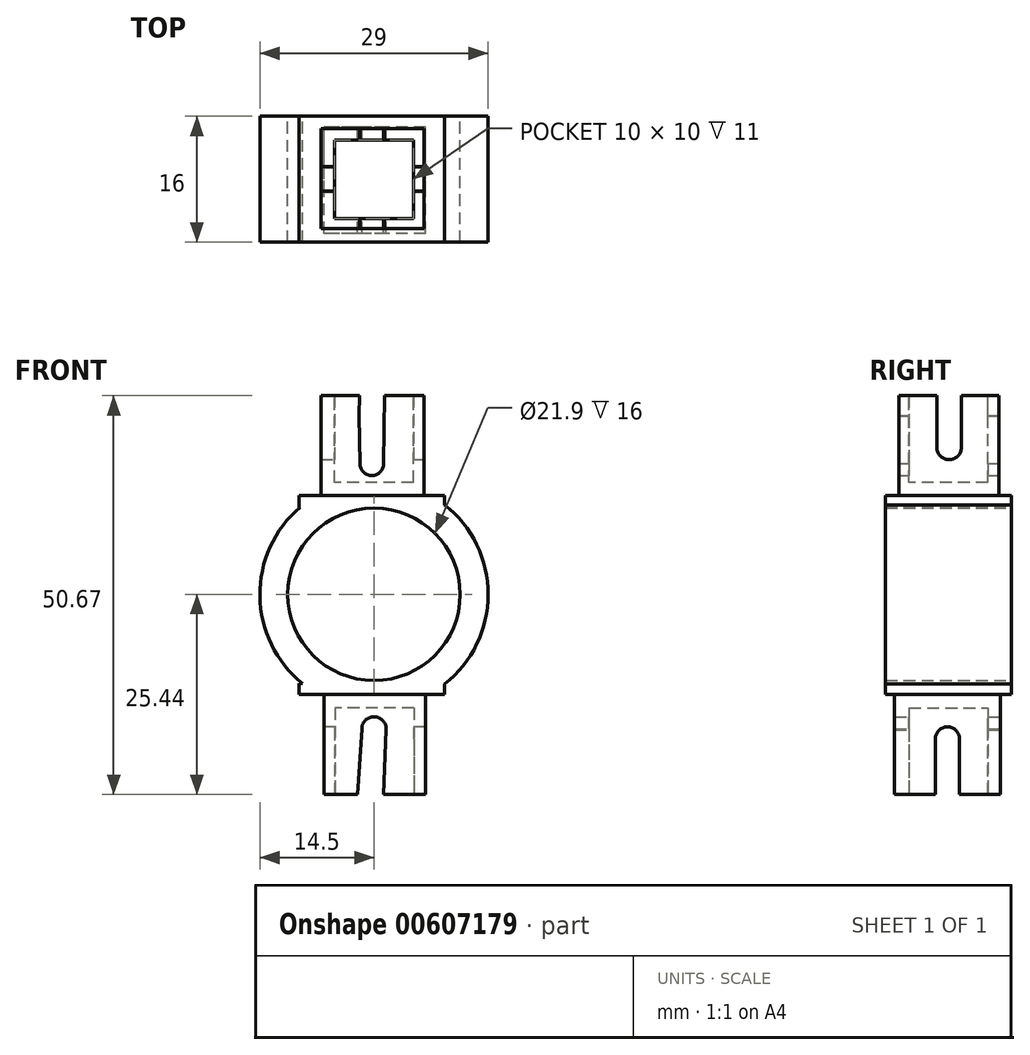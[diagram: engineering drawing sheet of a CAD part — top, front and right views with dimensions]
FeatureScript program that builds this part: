
annotation { "Feature Type Name" : "Feature", "Feature Type Description" : "" }
export const myFeature = defineFeature(function(context is Context, id is Id, definition is map)
    precondition{}
    {
        {
            var Q0;
            Q0=qCreatedBy(makeId("Front.planeOp"),FACE);
            var sketch = newSketch(context, id + "F0", { "sketchPlane" : qUnion([Q0])});
            skCircle(sketch, "E0", {"center": v(0, 0) * mm, "radius": 10.95 * mm});
            skCircle(sketch, "E1", {"center": v(0, 0) * mm, "radius": 14.5 * mm});
            skSolve(sketch);
        }
        {
            var Q0;
            Q0 = qSketchRegion(id + "F0", true);
            extrude(context, id + "F1", {"entities" : qUnion([Q0]), "depth" : 16 * mm, "offsetDistance" : 25.4 * mm});
        }
        {
            var Q0;
            Q0=qCreatedBy(makeId("Front.planeOp"),FACE);
            var sketch = newSketch(context, id + "F2", { "sketchPlane" : qUnion([Q0])});
            skLineSegment(sketch, "E2", {"start": v(8.98, 25.23) * mm, "end": v(-9.5, 25.23) * mm});
            skLineSegment(sketch, "E3", {"start": v(8.98, -25.44) * mm, "end": v(-9.5, -25.44) * mm});
            skLineSegment(sketch, "E4", {"start": v(8.98, -25.44) * mm, "end": v(8.98, -11.31) * mm});
            skLineSegment(sketch, "E5", {"start": v(8.98, -11.31) * mm, "end": v(-9.5, -11.31) * mm});
            skLineSegment(sketch, "E6", {"start": v(-9.5, -11.31) * mm, "end": v(-9.5, -25.44) * mm});
            skLineSegment(sketch, "E7", {"start": v(-9.5, 25.23) * mm, "end": v(-9.5, 11.06) * mm});
            skLineSegment(sketch, "E8", {"start": v(-9.5, 11.06) * mm, "end": v(8.98, 11.06) * mm});
            skLineSegment(sketch, "E9", {"start": v(8.98, 25.23) * mm, "end": v(8.98, 11.06) * mm});
            skSolve(sketch);
        }
        {
            var Q0;
            Q0 = qSketchRegion(id + "F2", true);
            extrude(context, id + "F3", {"entities" : qUnion([Q0]), "operationType" : NewBodyOperationType.ADD, "depth" : 16 * mm, "offsetDistance" : 25.4 * mm});
        }
        {
            var Q0;
            Q0=makeQuery(id+"F3.opExtrude","SWEPT_FACE",FACE,{"disambiguationData":[OSD([sQuery(id+"F2.wireOp",EDGE,"E2")])]});
            var sketch = newSketch(context, id + "F4", { "sketchPlane" : qUnion([Q0])});
            skPoint(sketch, "E10.endSnap0", {"position": v(0, -8) * mm});
            skLineSegment(sketch, "E11", {"start": v(5, -3) * mm, "end": v(-5, -3) * mm});
            skLineSegment(sketch, "E12", {"start": v(-5, -3) * mm, "end": v(-5, -13) * mm});
            skLineSegment(sketch, "E13", {"start": v(-5, -13) * mm, "end": v(5, -13) * mm});
            skLineSegment(sketch, "E14", {"start": v(5, -3) * mm, "end": v(5, -13) * mm});
            skSolve(sketch);
        }
        {
            var Q0;
            Q0=makeQuery(id+"F4.imprint","IMPRINT",FACE,{"disambiguationData":[TD([[makeQuery(id+"F4.imprint","IMPRINT",EDGE,{"derivedFrom":sQuery(id+"F4.wireOp",EDGE,"E11")}),1.0]])]});
            extrude(context, id + "F5", {"entities" : qUnion([Q0]), "operationType" : NewBodyOperationType.REMOVE, "oppositeDirection" : true, "depth" : 11 * mm, "offsetDistance" : 25.4 * mm});
        }
        {
            var Q0;
            Q0=makeQuery(id+"F3.opExtrude","SWEPT_FACE",FACE,{"disambiguationData":[OSD([sQuery(id+"F2.wireOp",EDGE,"E3")])]});
            var sketch = newSketch(context, id + "F6", { "sketchPlane" : qUnion([Q0])});
            skLineSegment(sketch, "E15", {"start": v(5.06, 3) * mm, "end": v(-4.94, 3) * mm});
            skLineSegment(sketch, "E16", {"start": v(-4.94, 3) * mm, "end": v(-4.94, 13) * mm});
            skLineSegment(sketch, "E17", {"start": v(-4.94, 13) * mm, "end": v(5.06, 13) * mm});
            skLineSegment(sketch, "E18", {"start": v(5.06, 13) * mm, "end": v(5.06, 3) * mm});
            skSolve(sketch);
        }
        {
            var Q0;
            Q0=makeQuery(id+"F6.imprint","IMPRINT",FACE,{"disambiguationData":[TD([[makeQuery(id+"F6.imprint","IMPRINT",EDGE,{"derivedFrom":sQuery(id+"F6.wireOp",EDGE,"E15")}),-1.0]])]});
            extrude(context, id + "F7", {"entities" : qUnion([Q0]), "operationType" : NewBodyOperationType.REMOVE, "oppositeDirection" : true, "depth" : 11 * mm, "offsetDistance" : 25.4 * mm});
        }
        {
            var Q0;
            Q0=makeQuery(id+"F3.boolean.opBoolean","MERGE",FACE,{"derivedFrom":[makeQuery(id+"F1.opExtrude","CAP_FACE",FACE,{"disambiguationData":[OSD([sQuery(id+"F0.wireOp",EDGE,"E0"),sQuery(id+"F0.wireOp",EDGE,"E1")])],"isStart":true}),makeQuery(id+"F3.opExtrude","CAP_FACE",FACE,{"disambiguationData":[OSD([sQuery(id+"F2.wireOp",EDGE,"eH45evdz-iIwl-7jf8-y0Qc-zG70ZCJFTtKG"),sQuery(id+"F2.wireOp",EDGE,"HCZmyl0s-dnjr-17Lv-xYgd-DPgU2AlNItuF"),sQuery(id+"F2.wireOp",EDGE,"E2"),sQuery(id+"F2.wireOp",EDGE,"hPoFIIJm-8yd8-o4Oi-e4Zf-j4DHxFpqQtic")])],"isStart":true}),makeQuery(id+"F3.opExtrude","CAP_FACE",FACE,{"disambiguationData":[OSD([sQuery(id+"F2.wireOp",EDGE,"RbHUidU9-xBkk-JISF-JKv2-oYIgWw0HqkPW"),sQuery(id+"F2.wireOp",EDGE,"OEjLOqE8-G3Si-yKOq-AH2c-0T68z6jIxc7M"),sQuery(id+"F2.wireOp",EDGE,"E3"),sQuery(id+"F2.wireOp",EDGE,"9qHgMatV-1gXa-NpmR-9eBD-IW0k8XRva2HU")])],"isStart":true})]});
            var sketch = newSketch(context, id + "F8", { "sketchPlane" : qUnion([Q0])});
            skArc(sketch, "E19", {"start": v(1.87, 22.63) * mm, "mid": v(1.87, 22.68) * mm, "end": v(1.87, 22.74) * mm});
            skArc(sketch, "E20", {"start": v(-1.23, 16.6) * mm, "mid": v(0.27, 15.1) * mm, "end": v(1.77, 16.6) * mm});
            skArc(sketch, "E21", {"start": v(1.55, -17.1) * mm, "mid": v(-0.07, -15.55) * mm, "end": v(-1.54, -17.23) * mm});
            skLineSegment(sketch, "E22", {"start": v(-1.55, -17.1) * mm, "end": v(-1.18, -25.44) * mm});
            skLineSegment(sketch, "E23", {"start": v(1.55, -17.1) * mm, "end": v(2.1, -25.44) * mm});
            skLineSegment(sketch, "E24", {"start": v(-1.18, -25.44) * mm, "end": v(2.1, -25.44) * mm});
            skLineSegment(sketch, "E25", {"start": v(-1.23, 16.6) * mm, "end": v(-1.37, 25.23) * mm});
            skLineSegment(sketch, "E26", {"start": v(1.77, 16.6) * mm, "end": v(1.87, 22.68) * mm});
            skLineSegment(sketch, "E27", {"start": v(1.87, 22.68) * mm, "end": v(1.83, 25.23) * mm});
            skLineSegment(sketch, "E28", {"start": v(1.83, 25.23) * mm, "end": v(-1.37, 25.23) * mm});
            skSolve(sketch);
        }
        {
            var Q0;
            Q0 = qSketchRegion(id + "F8", true);
            extrude(context, id + "F9", {"entities" : qUnion([Q0]), "operationType" : NewBodyOperationType.REMOVE, "oppositeDirection" : true, "depth" : 25.4 * mm, "offsetDistance" : 25.4 * mm});
        }
        {
            var Q0;
            Q0=makeQuery(id+"F3.opExtrude","SWEPT_FACE",FACE,{"disambiguationData":[OSD([sQuery(id+"F2.wireOp",EDGE,"E2")])]});
            var sketch = newSketch(context, id + "F10", { "sketchPlane" : qUnion([Q0])});
            skLineSegment(sketch, "E29.bottom", {"start": v(8.98, 0) * mm, "end": v(8.98, 0) * mm});
            skLineSegment(sketch, "E29.top", {"start": v(8.98, -16) * mm, "end": v(8.98, -16) * mm});
            skLineSegment(sketch, "E29.left", {"start": v(8.98, 0) * mm, "end": v(8.98, -16) * mm});
            skLineSegment(sketch, "E29.right", {"start": v(8.98, 0) * mm, "end": v(8.98, -16) * mm});
            skLineSegment(sketch, "E30", {"start": v(8.98, -16) * mm, "end": v(-9.5, -16) * mm});
            skLineSegment(sketch, "E31", {"start": v(-9.5, -16) * mm, "end": v(-9.5, 0) * mm});
            skLineSegment(sketch, "E32", {"start": v(-9.5, 0) * mm, "end": v(8.98, 0) * mm});
            skLineSegment(sketch, "E33", {"start": v(-5, -3) * mm, "end": v(5, -3) * mm});
            skLineSegment(sketch, "E34", {"start": v(-6.75, -14.27) * mm, "end": v(-6.75, -1.58) * mm});
            skLineSegment(sketch, "E35", {"start": v(-6.75, -1.58) * mm, "end": v(6.37, -1.58) * mm});
            skLineSegment(sketch, "E36", {"start": v(6.37, -1.58) * mm, "end": v(6.37, -14.27) * mm});
            skLineSegment(sketch, "E37", {"start": v(-6.75, -14.27) * mm, "end": v(6.37, -14.27) * mm});
            skSolve(sketch);
        }
        {
            var Q0;
            Q0 = qSketchRegion(id + "F10", true);
            extrude(context, id + "F11", {"entities" : qUnion([Q0]), "operationType" : NewBodyOperationType.REMOVE, "oppositeDirection" : true, "depth" : 12.7 * mm, "offsetDistance" : 25.4 * mm});
        }
        {
            var Q0;
            Q0=makeQuery(id+"F3.opExtrude","SWEPT_FACE",FACE,{"disambiguationData":[OSD([sQuery(id+"F2.wireOp",EDGE,"E3")])]});
            var sketch = newSketch(context, id + "F12", { "sketchPlane" : qUnion([Q0])});
            skLineSegment(sketch, "E38", {"start": v(8.98, 16) * mm, "end": v(8.98, 0) * mm});
            skLineSegment(sketch, "E39", {"start": v(8.98, 0) * mm, "end": v(8.98, 0) * mm});
            skLineSegment(sketch, "E40", {"start": v(8.98, 0) * mm, "end": v(8.98, 16) * mm});
            skLineSegment(sketch, "E41", {"start": v(8.98, 16) * mm, "end": v(8.98, 16) * mm});
            skLineSegment(sketch, "E42", {"start": v(6.57, 14.88) * mm, "end": v(-6.32, 14.88) * mm});
            skLineSegment(sketch, "E43", {"start": v(8.98, 0) * mm, "end": v(-9.5, 0) * mm});
            skLineSegment(sketch, "E44", {"start": v(-9.5, 0) * mm, "end": v(-9.5, 16) * mm});
            skLineSegment(sketch, "E45", {"start": v(-9.5, 16) * mm, "end": v(8.98, 16) * mm});
            skLineSegment(sketch, "E46", {"start": v(6.57, 14.88) * mm, "end": v(6.57, 1.4) * mm});
            skLineSegment(sketch, "E47", {"start": v(6.57, 1.4) * mm, "end": v(-6.32, 1.4) * mm});
            skLineSegment(sketch, "E48", {"start": v(-6.32, 14.88) * mm, "end": v(-6.32, 1.4) * mm});
            skSolve(sketch);
        }
        {
            var Q0;
            Q0 = qSketchRegion(id + "F12", true);
            extrude(context, id + "F13", {"entities" : qUnion([Q0]), "operationType" : NewBodyOperationType.REMOVE, "oppositeDirection" : true, "depth" : 12.7 * mm, "offsetDistance" : 25.4 * mm});
        }
        {
            var Q0;
            Q0=makeQuery(id+"F11.boolean.opBoolean","COPY",FACE,{"derivedFrom":makeQuery(id+"F11.opExtrude","SWEPT_FACE",FACE,{"disambiguationData":[OSD([sQuery(id+"F10.wireOp",EDGE,"E36")])]})});
            var sketch = newSketch(context, id + "F14", { "sketchPlane" : qUnion([Q0])});
            skPoint(sketch, "E49.centerSnap0", {"position": v(-7.92, 25.23) * mm});
            skArc(sketch, "E50", {"start": v(-9.47, 18.65) * mm, "mid": v(-7.92, 17.1) * mm, "end": v(-6.37, 18.65) * mm});
            skLineSegment(sketch, "E51", {"start": v(-9.47, 18.65) * mm, "end": v(-9.47, 25.23) * mm});
            skLineSegment(sketch, "E52", {"start": v(-6.37, 18.65) * mm, "end": v(-6.37, 25.23) * mm});
            skLineSegment(sketch, "E53", {"start": v(-6.37, 25.23) * mm, "end": v(-9.47, 25.23) * mm});
            skPoint(sketch, "E49.center.orphan", {"position": v(-7.92, 22.95) * mm});
            skSolve(sketch);
        }
        {
            var Q0;
            Q0 = qSketchRegion(id + "F14", true);
            extrude(context, id + "F15", {"entities" : qUnion([Q0]), "operationType" : NewBodyOperationType.REMOVE, "oppositeDirection" : true, "depth" : 25.4 * mm, "offsetDistance" : 25.4 * mm});
        }
        {
            var Q0;
            Q0=makeQuery(id+"F13.boolean.opBoolean","COPY",FACE,{"derivedFrom":makeQuery(id+"F13.opExtrude","SWEPT_FACE",FACE,{"disambiguationData":[OSD([sQuery(id+"F12.wireOp",EDGE,"E48")])]})});
            var sketch = newSketch(context, id + "F16", { "sketchPlane" : qUnion([Q0])});
            skPoint(sketch, "E54.centerSnap0", {"position": v(8.14, -25.44) * mm});
            skArc(sketch, "E55", {"start": v(9.69, -18.38) * mm, "mid": v(8.14, -16.83) * mm, "end": v(6.59, -18.38) * mm});
            skLineSegment(sketch, "E56", {"start": v(6.59, -18.38) * mm, "end": v(6.59, -25.44) * mm});
            skLineSegment(sketch, "E57", {"start": v(9.69, -18.38) * mm, "end": v(9.69, -25.44) * mm});
            skLineSegment(sketch, "E58", {"start": v(9.69, -25.44) * mm, "end": v(6.59, -25.44) * mm});
            skPoint(sketch, "E54.center.orphan", {"position": v(8.14, -22.55) * mm});
            skSolve(sketch);
        }
        {
            var Q0;
            Q0=makeQuery(id+"F16.imprint","IMPRINT",FACE,{"disambiguationData":[TD([[makeQuery(id+"F16.imprint","IMPRINT",EDGE,{"derivedFrom":sQuery(id+"F16.wireOp",EDGE,"E55")}),1.0]])]});
            extrude(context, id + "F17", {"entities" : qUnion([Q0]), "operationType" : NewBodyOperationType.REMOVE, "oppositeDirection" : true, "depth" : 25.4 * mm, "offsetDistance" : 25.4 * mm});
        }
    });
